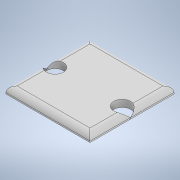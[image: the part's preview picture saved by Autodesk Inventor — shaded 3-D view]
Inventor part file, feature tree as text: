
AUTODESK INVENTOR PART (.ipt)
format: ipt  version: 2020 (Build 240168000, 168)  size: 124,928 bytes
history: native  units: in
note: dims shown in document units (in); Inventor stores cm internally (conversion verified against a paired STEP export)
features: sketch x2, extrude x1, fillet x1, hole x1
ambient origin geometry x8: Origin, YZ Plane, XZ Plane, XY Plane, X Axis, Y Axis, Z Axis, Center Point
bodies: Solid1 (feature_tree)
feature tree (5):
  extrude  "Extrusion1"  Depth=0.6in
  sketch  "Sketch2"  dims[d4=0.06in d5=0.31in d6=0.06in d7=0.31in d15=0.04in d17=0.12in d18=0.75in d19=0.4in d20=0.15in d21=0.5635in d22=1.0in d23=0.8108in]
  fillet  "Fillet1"  Radius=0.05in
  hole  "Hole2"  [1 undecoded]
  sketch  "Sketch1"  dims[d0=0.6in d1=0.6in d2=0.05in d3=0.0in]
note: 1 required parameter value undecoded (feature->parameter linkage not recoverable at this tier; creation-order binding heuristic only, values carry confidence <= 0.55)
